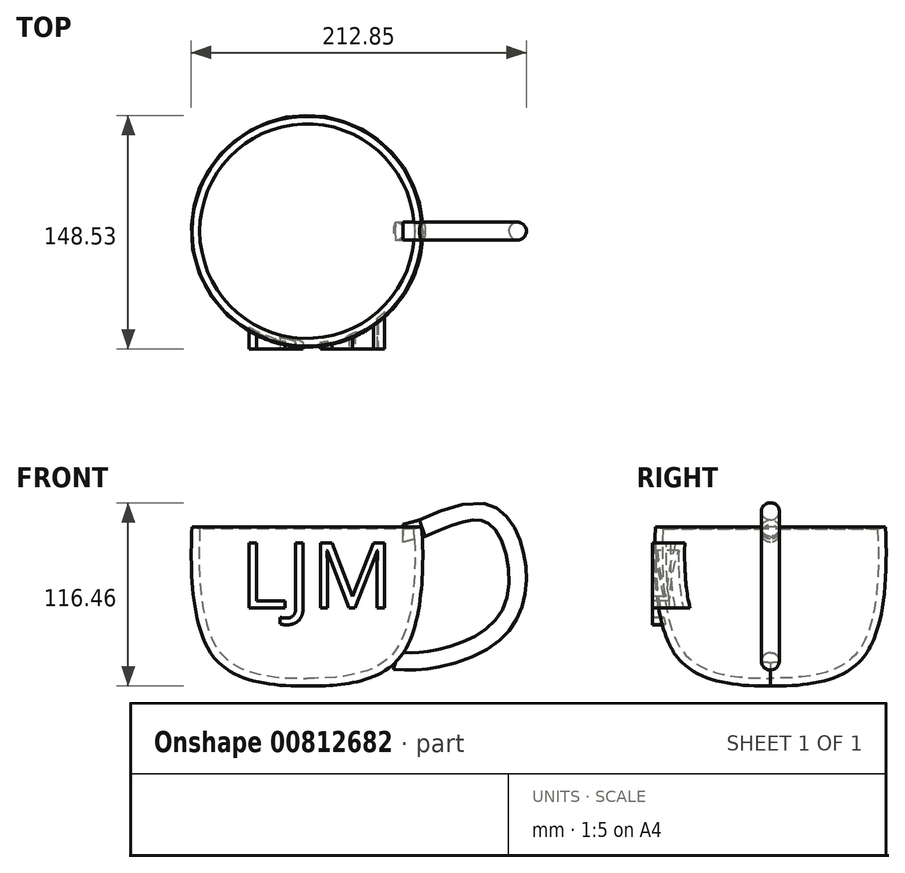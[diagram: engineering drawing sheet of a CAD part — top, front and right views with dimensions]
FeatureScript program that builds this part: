
annotation { "Feature Type Name" : "Feature", "Feature Type Description" : "" }
export const myFeature = defineFeature(function(context is Context, id is Id, definition is map)
    precondition{}
    {
        {
            var Q0;
            Q0=qCreatedBy(makeId("Front.planeOp"),FACE);
            var sketch = newSketch(context, id + "F0", { "sketchPlane" : qUnion([Q0])});
            skFitSpline(sketch, "E0", {"points": [v(71.25, 71.53) * mm, v(73.22, 17.85) * mm, v(58.89, -34.71) * mm, v(27.69, -50.73) * mm, v(0, -52.7) * mm], "startDerivative": vector(15.52, -183.33) * mm, "endDerivative": vector(-131.71, -1.3) * mm});
            skLineSegment(sketch, "E1", {"start": v(0, 75.75) * mm, "end": v(0, -74.63) * mm});
            skFitSpline(sketch, "E2.0", {"points": [v(66.27, 71.11) * mm, v(66.6, 67.3) * mm, v(67.24, 59.68) * mm, v(68.04, 48.2) * mm, v(68.45, 38.51) * mm, v(68.55, 30.6) * mm, v(68.49, 24.59) * mm, v(68.27, 18.46) * mm, v(67.88, 12.22) * mm, v(67.3, 5.95) * mm, v(66.2, -2.33) * mm, v(64.6, -10.3) * mm, v(62.4, -17.6) * mm, v(60.43, -22.64) * mm, v(58.52, -26.4) * mm, v(56.84, -29.1) * mm, v(55.5, -30.98) * mm, v(54.08, -32.68) * mm, v(52.56, -34.26) * mm, v(50.95, -35.73) * mm, v(48.68, -37.52) * mm, v(45.63, -39.5) * mm, v(41.69, -41.5) * mm, v(37.53, -43.12) * mm, v(33.24, -44.42) * mm, v(29.63, -45.27) * mm, v(26.75, -45.83) * mm, v(23.9, -46.32) * mm, v(20.4, -46.79) * mm, v(14.9, -47.31) * mm, v(8.12, -47.62) * mm, v(2.7, -47.67) * mm, v(-0.05, -47.7) * mm]});
            skLineSegment(sketch, "E3", {"start": v(60.85, 69.57) * mm, "end": v(79.68, 69.57) * mm});
            skFitSpline(sketch, "E4", {"points": [v(72.99, 48.4) * mm, v(119.78, 55.23) * mm, v(129.9, -6.6) * mm, v(80.43, -36.4) * mm, v(56.33, -37.54) * mm], "startDerivative": vector(208.27, 92.72) * mm, "endDerivative": vector(-114.97, 5.5) * mm});
            skLineSegment(sketch, "E5", {"start": v(72.99, 48.4) * mm, "end": v(61.1, 45.21) * mm});
            skSolve(sketch);
        }
        {
            var Q0;
            {var subQ0=sQuery(id+"F0.wireOp",EDGE,"E1");var subQ1=sQuery(id+"F0.wireOp",EDGE,"E0");var subQ2=makeQuery(id+"F0.imprint","INTERSECT",VERTEX,{"derivedFrom":[subQ1,subQ0]});Q0=makeQuery(id+"F0.imprint","IMPRINT",FACE,{"disambiguationData":[TD([[makeQuery(id+"F0.imprint","IMPRINT",EDGE,{"disambiguationData":[TD([[subQ2,1.0]])],"derivedFrom":subQ1}),-1.0]])]});}
            var Q1;
            Q1=sQuery(id+"F0.wireOp",EDGE,"E1");
            revolve(context, id + "F1", {"surfaceOperationType" : NewSurfaceOperationType.NEW, "entities" : qUnion([Q0]), "axis" : qUnion([Q1]), "revolveType" : RevolveType.FULL});
        }
        {
            var Q0;
            Q0=qCreatedBy(makeId("Front.planeOp"),FACE);
            cPlane(context, id + "F2", {"entities" : qUnion([Q0]), "cplaneType" : CPlaneType.OFFSET, "offset" : 75 * mm, "width" : 150 * mm, "height" : 150 * mm});
        }
        {
            var Q0;
            Q0=qCreatedBy(id+"F2.planeOp",FACE);
            var sketch = newSketch(context, id + "F3", { "sketchPlane" : qUnion([Q0])});
            skText(sketch, "E6", { "text": "LJM", "fontName": "OpenSans-Regular.ttf"});
            const initialGuessF3  = {"E6": [-0.04258, -0.00295, 1, 0, 0.0416]};
            skSetInitialGuess(sketch, initialGuessF3);
            skSolve(sketch);
        }
        {
            var Q0;
            Q0 = qSketchRegion(id + "F3", true);
            extrude(context, id + "F4", {"entities" : qUnion([Q0]), "operationType" : NewBodyOperationType.ADD, "endBound" : BoundingType.UP_TO_NEXT, "oppositeDirection" : true, "depth" : 25 * mm, "offsetDistance" : 25 * mm});
        }
        {
            var Q0;
            Q0=qCreatedBy(makeId("Right.planeOp"),FACE);
            cPlane(context, id + "F5", {"entities" : qUnion([Q0]), "cplaneType" : CPlaneType.OFFSET, "offset" : 65 * mm, "width" : 150 * mm, "height" : 150 * mm});
        }
        {
            var Q0;
            Q0=qCreatedBy(id+"F5.planeOp",FACE);
            var sketch = newSketch(context, id + "F6", { "sketchPlane" : qUnion([Q0])});
            skCircle(sketch, "E7", {"center": v(0, 45.4) * mm, "radius": 5.69 * mm});
            skSolve(sketch);
        }
        {
            var Q0;
            Q0=makeQuery(id+"F6.imprint","IMPRINT",FACE,{"disambiguationData":[TD([[makeQuery(id+"F6.imprint","IMPRINT",EDGE,{"derivedFrom":sQuery(id+"F6.wireOp",EDGE,"E7")}),1.0]])]});
            var Q1;
            Q1=sQuery(id+"F0.wireOp",EDGE,"E4");
            var Q2;
            Q2=sQuery(id+"F0.wireOp",EDGE,"E5");
            sweep(context, id + "F7", {"operationType" : NewBodyOperationType.ADD, "profiles" : qUnion([Q0]), "path" : qUnion([Q1, Q2])});
        }
    });
